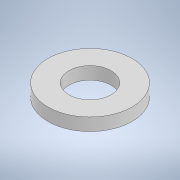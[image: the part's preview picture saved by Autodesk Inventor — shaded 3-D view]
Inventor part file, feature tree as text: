
AUTODESK INVENTOR PART (.ipt)
format: ipt  version: 2022.2 (Build 262287000, 287)  size: 97,792 bytes
history: native  units: mm
features: extrude x1, sketch x1
ambient origin geometry x8: Origin, YZ Plane, XZ Plane, XY Plane, X Axis, Y Axis, Z Axis, Center Point
bodies: Solid1 (feature_tree)
feature tree (2):
  extrude  "Extrusion1"  Depth=10.0mm
  sketch  "Sketch1"  dims[d0=5.0mm d1=10.0mm d2=1.5mm d3=0.0mm]
